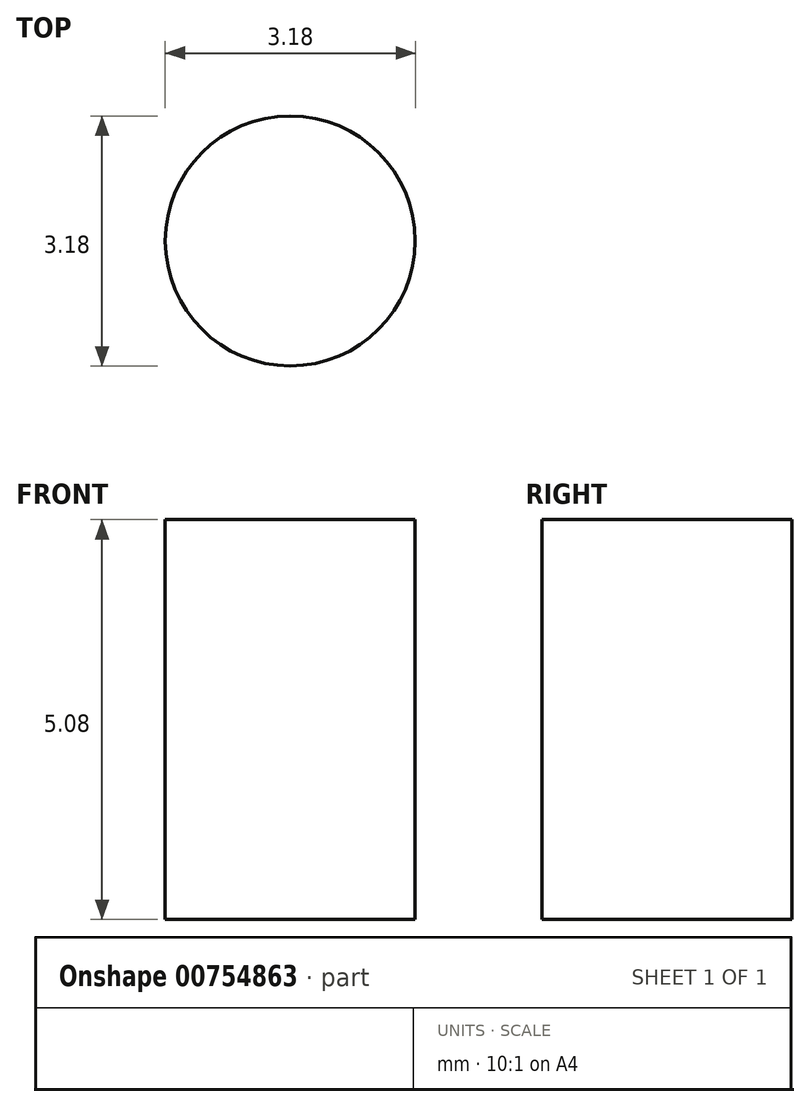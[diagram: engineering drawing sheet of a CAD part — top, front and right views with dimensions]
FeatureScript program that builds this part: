
annotation { "Feature Type Name" : "Feature", "Feature Type Description" : "" }
export const myFeature = defineFeature(function(context is Context, id is Id, definition is map)
    precondition{}
    {
        {
            var Q0;
            Q0=qCreatedBy(makeId("Top.planeOp"),FACE);
            var sketch = newSketch(context, id + "F0", { "sketchPlane" : qUnion([Q0])});
            skCircle(sketch, "E0", {"center": v(-100, -25.49) * mm, "radius": 1.59 * mm});
            skSolve(sketch);
        }
        {
            var Q0;
            Q0=makeQuery(id+"F0.imprint","IMPRINT",FACE,{"disambiguationData":[TD([[makeQuery(id+"F0.imprint","IMPRINT",EDGE,{"derivedFrom":sQuery(id+"F0.wireOp",EDGE,"E0")}),1.0]])]});
            extrude(context, id + "F1", {"entities" : qUnion([Q0]), "depth" : 5.08 * mm, "offsetDistance" : 25.4 * mm});
        }
    });
